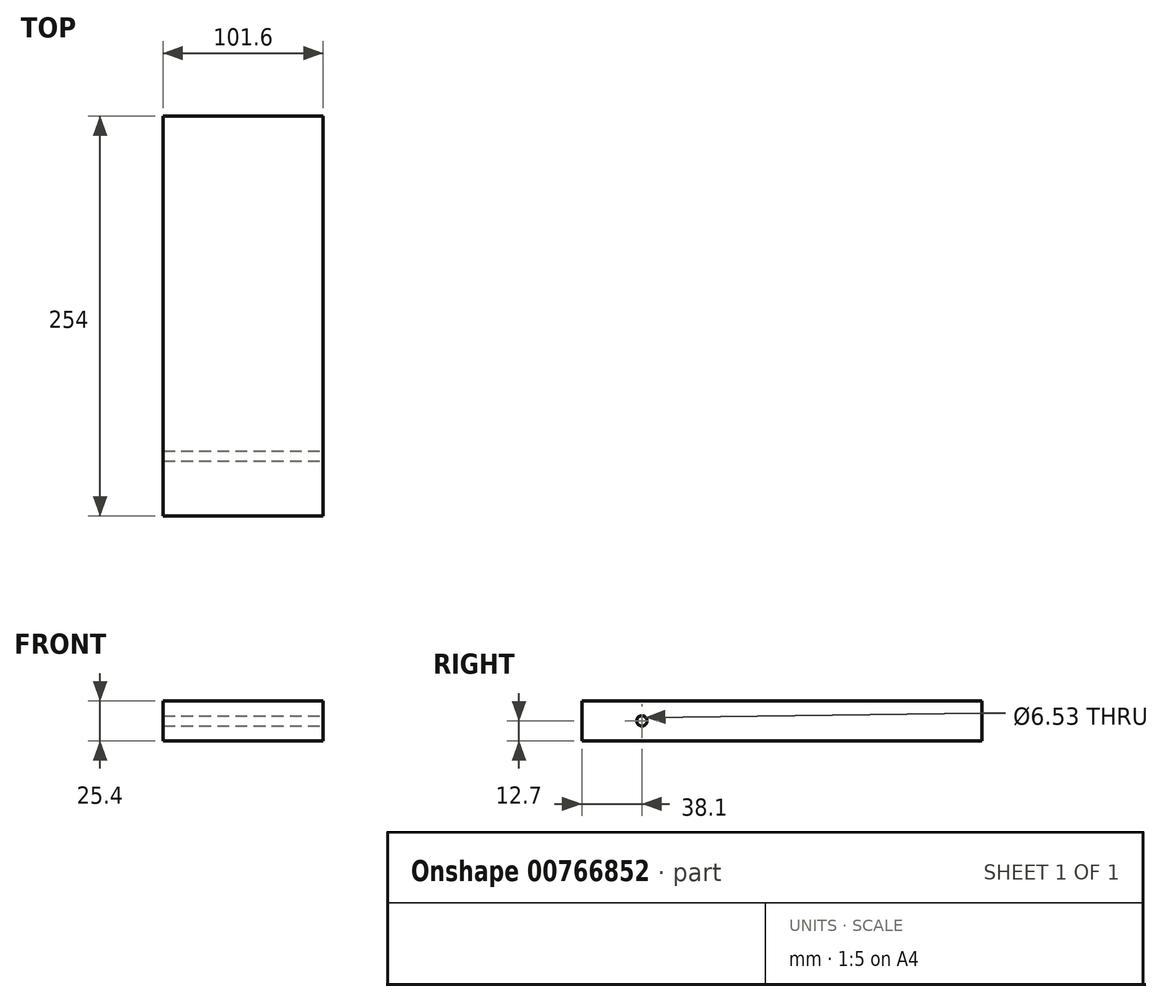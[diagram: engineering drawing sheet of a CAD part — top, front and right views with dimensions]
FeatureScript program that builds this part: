
annotation { "Feature Type Name" : "Feature", "Feature Type Description" : "" }
export const myFeature = defineFeature(function(context is Context, id is Id, definition is map)
    precondition{}
    {
        {
            var Q0;
            Q0=qCreatedBy(makeId("Top.planeOp"),FACE);
            var sketch = newSketch(context, id + "F0", { "sketchPlane" : qUnion([Q0])});
            skLineSegment(sketch, "E0.bottom", {"start": v(50.8, 127) * mm, "end": v(-50.8, 127) * mm});
            skLineSegment(sketch, "E0.top", {"start": v(50.8, -127) * mm, "end": v(-50.8, -127) * mm});
            skLineSegment(sketch, "E0.left", {"start": v(50.8, 127) * mm, "end": v(50.8, -127) * mm});
            skLineSegment(sketch, "E0.right", {"start": v(-50.8, 127) * mm, "end": v(-50.8, -127) * mm});
            skPoint(sketch, "E0.middle", {"position": v(0, 0) * mm});
            skSolve(sketch);
        }
        {
            var Q0;
            Q0=makeQuery(id+"F0.imprint","IMPRINT",FACE,{"disambiguationData":[TD([[makeQuery(id+"F0.imprint","IMPRINT",EDGE,{"derivedFrom":sQuery(id+"F0.wireOp",EDGE,"E0.bottom")}),1.0]])]});
            extrude(context, id + "F1", {"entities" : qUnion([Q0]), "depth" : 25.4 * mm, "offsetDistance" : 25.4 * mm});
        }
        {
            var Q0;
            Q0=makeQuery(id+"F1.opExtrude","SWEPT_FACE",FACE,{"disambiguationData":[OSD([sQuery(id+"F0.wireOp",EDGE,"E0.left")])]});
            var sketch = newSketch(context, id + "F2", { "sketchPlane" : qUnion([Q0])});
            skLineSegment(sketch, "E1", {"start": v(-127, 12.7) * mm, "end": v(-88.9, 12.7) * mm});
            skCircle(sketch, "E2", {"center": v(-88.9, 12.7) * mm, "radius": 6.35 * mm});
            skSolve(sketch);
        }
        {
            var Q0;
            Q0=sQuery(id+"F2.wireOp",VERTEX,"E2.center");
            var Q1;
            Q1=makeQuery(id+"F1.opExtrude","SWEPT_BODY",BODY,{"disambiguationData":[OSD([sQuery(id+"F0.wireOp",EDGE,"E0.bottom"),sQuery(id+"F0.wireOp",EDGE,"E0.top"),sQuery(id+"F0.wireOp",EDGE,"E0.left"),sQuery(id+"F0.wireOp",EDGE,"E0.right")])]});
            hole(context, id + "F3", {"style" : HoleStyle.SIMPLE, "endStyle" : HoleEndStyle.THROUGH, "standardTappedOrClearance" : lookupTablePath({ "standard" : "ANSI", "engagement" : "75%", "pitch" : "18 tpi", "size" : "5/16", "type" : "Tapped" }), "standardBlindInLast" : lookupTablePath({ "standard" : "ANSI", "engagement" : "75%", "pitch" : "18 tpi", "size" : "5/16", "type" : "Tapped" }), "holeDiameter" : 6.53 * mm, "majorDiameter" : 7.94 * mm, "showTappedDepth" : true, "isTappedThrough" : true, "tappedDepth" : 12.7 * mm, "tapClearance" : 3, "startFromSketch" : true, "locations" : qUnion([Q0]), "scope" : qUnion([Q1])});
        }
    });
